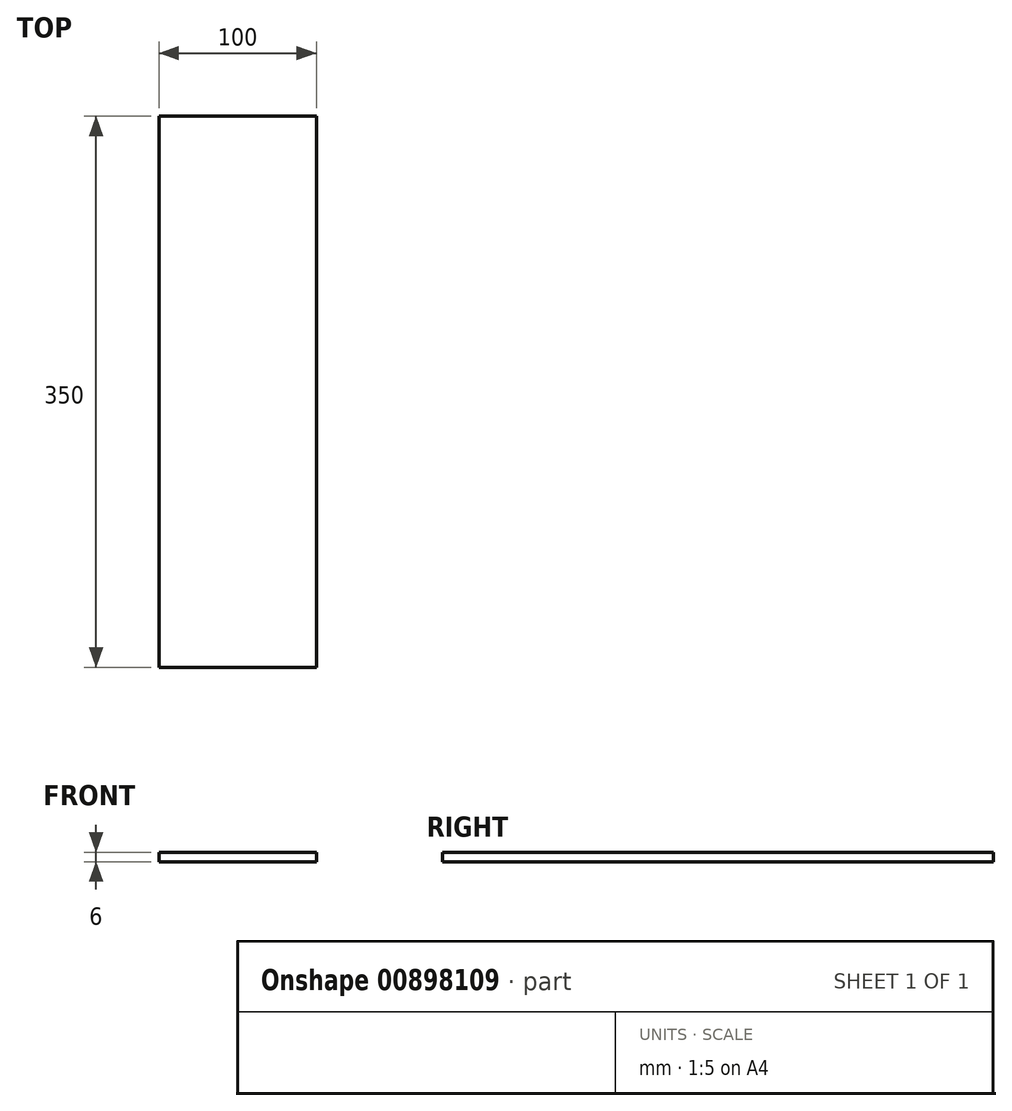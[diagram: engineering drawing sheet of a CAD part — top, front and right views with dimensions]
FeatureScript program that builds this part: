
annotation { "Feature Type Name" : "Feature", "Feature Type Description" : "" }
export const myFeature = defineFeature(function(context is Context, id is Id, definition is map)
    precondition{}
    {
        {
            var Q0;
            Q0=qCreatedBy(makeId("Front.planeOp"),FACE);
            var sketch = newSketch(context, id + "F0", { "sketchPlane" : qUnion([Q0])});
            skLineSegment(sketch, "E0.bottom", {"start": v(0, 0) * mm, "end": v(100, 0) * mm});
            skLineSegment(sketch, "E0.top", {"start": v(0, 6) * mm, "end": v(100, 6) * mm});
            skLineSegment(sketch, "E0.left", {"start": v(0, 0) * mm, "end": v(0, 6) * mm});
            skLineSegment(sketch, "E0.right", {"start": v(100, 0) * mm, "end": v(100, 6) * mm});
            skSolve(sketch);
        }
        {
            var Q0;
            Q0 = qSketchRegion(id + "F0", true);
            extrude(context, id + "F1", {"entities" : qUnion([Q0]), "depth" : 350 * mm, "offsetDistance" : 25 * mm});
        }
    });
